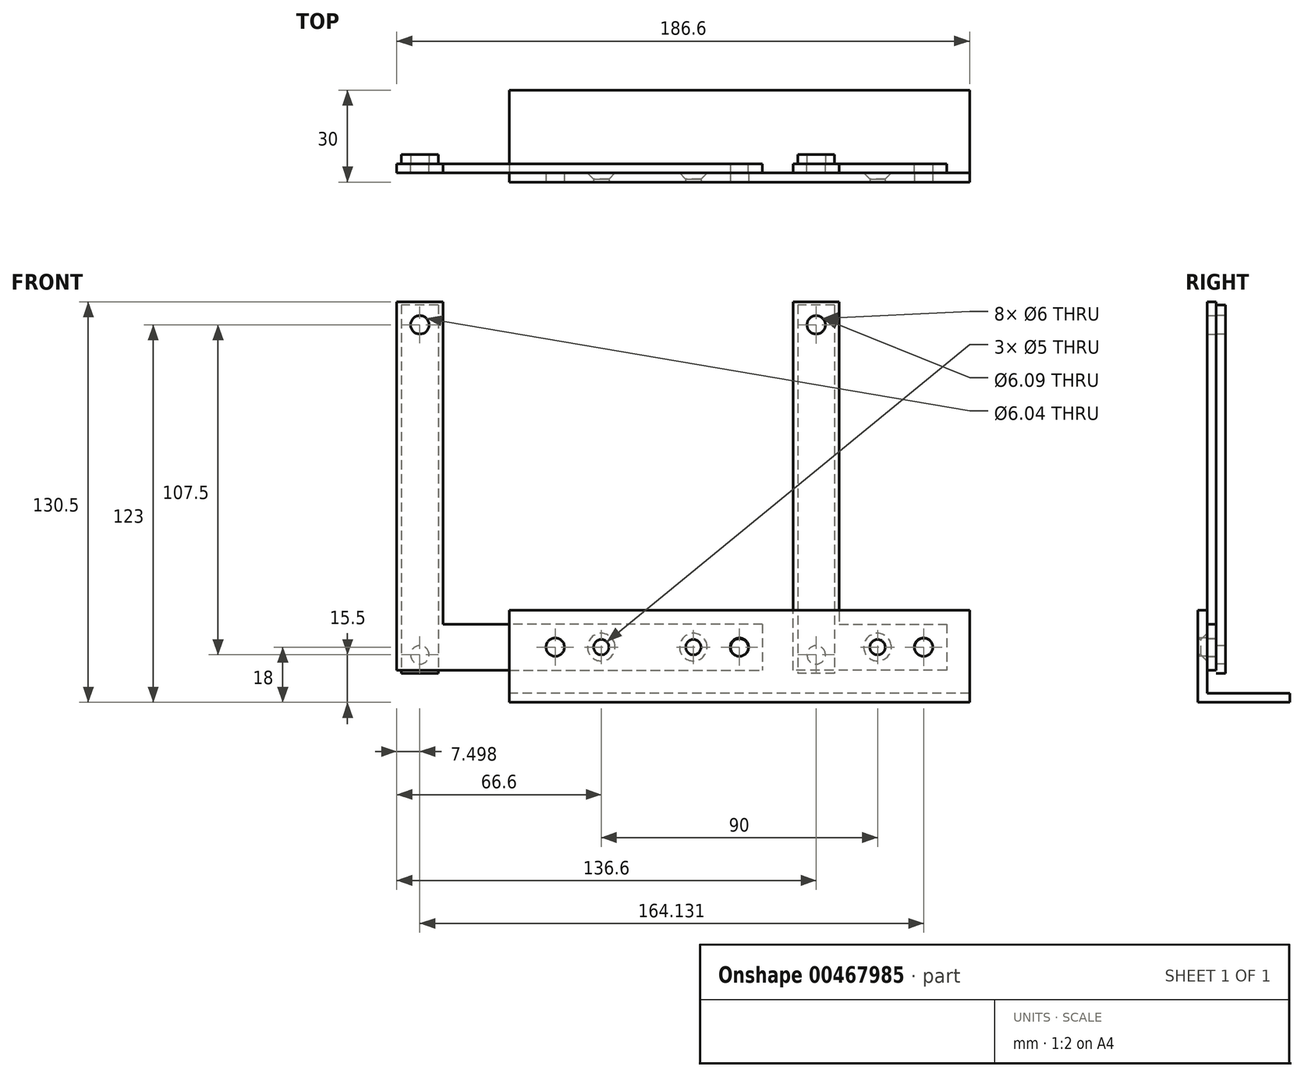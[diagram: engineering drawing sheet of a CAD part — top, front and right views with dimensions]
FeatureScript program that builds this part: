
annotation { "Feature Type Name" : "Feature", "Feature Type Description" : "" }
export const myFeature = defineFeature(function(context is Context, id is Id, definition is map)
    precondition{}
    {
        {
            var Q0;
            Q0=qCreatedBy(makeId("Right.planeOp"),FACE);
            var sketch = newSketch(context, id + "F0", { "sketchPlane" : qUnion([Q0])});
            skLineSegment(sketch, "E0", {"start": v(-6, 30) * mm, "end": v(-6, 0) * mm});
            skLineSegment(sketch, "E1", {"start": v(-6, 0) * mm, "end": v(24, 0) * mm});
            skLineSegment(sketch, "E2", {"start": v(24, 0) * mm, "end": v(24, 3) * mm});
            skLineSegment(sketch, "E3", {"start": v(24, 3) * mm, "end": v(-3, 3) * mm});
            skLineSegment(sketch, "E4", {"start": v(-3, 3) * mm, "end": v(-3, 30) * mm});
            skLineSegment(sketch, "E5", {"start": v(-3, 30) * mm, "end": v(-6, 30) * mm});
            skSolve(sketch);
        }
        {
            var Q0;
            Q0 = qSketchRegion(id + "F0", true);
            extrude(context, id + "F1", {"entities" : qUnion([Q0]), "depth" : 150 * mm});
        }
        {
            var Q0;
            Q0=qCreatedBy(makeId("Front.planeOp"),FACE);
            var sketch = newSketch(context, id + "F2", { "sketchPlane" : qUnion([Q0])});
            skCircle(sketch, "E6", {"center": v(135, 18) * mm, "radius": 3 * mm});
            skCircle(sketch, "E7", {"center": v(75, 18) * mm, "radius": 3 * mm});
            skCircle(sketch, "E8", {"center": v(15, 18) * mm, "radius": 3 * mm});
            skCircle(sketch, "E9", {"center": v(120, 18) * mm, "radius": 2.5 * mm});
            skCircle(sketch, "E10", {"center": v(30, 18) * mm, "radius": 2.5 * mm});
            skCircle(sketch, "E11", {"center": v(60, 18) * mm, "radius": 2.5 * mm});
            skSolve(sketch);
        }
        {
            var Q0;
            Q0 = qSketchRegion(id + "F2", true);
            extrude(context, id + "F3", {"entities" : qUnion([Q0]), "operationType" : NewBodyOperationType.REMOVE, "endBound" : BoundingType.SYMMETRIC, "oppositeDirection" : true, "depth" : 25 * mm});
        }
        {
            var Q0;
            Q0=makeQuery(id+"F3.boolean.opBoolean","INTERSECT",EDGE,{"derivedFrom":[makeQuery(id+"F1.opExtrude","SWEPT_FACE",FACE,{"disambiguationData":[OSD([sQuery(id+"F0.wireOp",EDGE,"E4")])]}),makeQuery(id+"F3.opExtrude","SWEPT_FACE",FACE,{"disambiguationData":[OSD([sQuery(id+"F2.wireOp",EDGE,"E11")])]})]});
            var Q1;
            Q1=makeQuery(id+"F3.boolean.opBoolean","INTERSECT",EDGE,{"derivedFrom":[makeQuery(id+"F1.opExtrude","SWEPT_FACE",FACE,{"disambiguationData":[OSD([sQuery(id+"F0.wireOp",EDGE,"E4")])]}),makeQuery(id+"F3.opExtrude","SWEPT_FACE",FACE,{"disambiguationData":[OSD([sQuery(id+"F2.wireOp",EDGE,"E10")])]})]});
            var Q2;
            Q2=makeQuery(id+"F3.boolean.opBoolean","INTERSECT",EDGE,{"derivedFrom":[makeQuery(id+"F1.opExtrude","SWEPT_FACE",FACE,{"disambiguationData":[OSD([sQuery(id+"F0.wireOp",EDGE,"E4")])]}),makeQuery(id+"F3.opExtrude","SWEPT_FACE",FACE,{"disambiguationData":[OSD([sQuery(id+"F2.wireOp",EDGE,"E9")])]})]});
            chamfer(context, id + "F4", {"entities" : qUnion([Q0, Q1, Q2]), "width" : 2 * mm, "tangentPropagation" : true});
        }
        {
            var Q0;
            Q0=qCreatedBy(makeId("Front.planeOp"),FACE);
            var sketch = newSketch(context, id + "F5", { "sketchPlane" : qUnion([Q0])});
            skLineSegment(sketch, "E12", {"start": v(142.5, 25.5) * mm, "end": v(142.5, 10.5) * mm});
            skLineSegment(sketch, "E13", {"start": v(142.5, 10.5) * mm, "end": v(92.5, 10.5) * mm});
            skLineSegment(sketch, "E14", {"start": v(92.5, 10.5) * mm, "end": v(92.5, 130.5) * mm});
            skLineSegment(sketch, "E15", {"start": v(92.5, 130.5) * mm, "end": v(107.5, 130.5) * mm});
            skLineSegment(sketch, "E16", {"start": v(107.5, 130.5) * mm, "end": v(107.5, 25.5) * mm});
            skLineSegment(sketch, "E17", {"start": v(107.5, 25.5) * mm, "end": v(142.5, 25.5) * mm});
            skCircle(sketch, "E18", {"center": v(135.03, 17.92) * mm, "radius": 3 * mm});
            skLineSegment(sketch, "E19", {"start": v(82.5, 25.5) * mm, "end": v(82.5, 10.5) * mm});
            skLineSegment(sketch, "E20", {"start": v(82.5, 25.5) * mm, "end": v(-21.6, 25.5) * mm});
            skLineSegment(sketch, "E21", {"start": v(-21.6, 25.5) * mm, "end": v(-21.6, 130.5) * mm});
            skLineSegment(sketch, "E22", {"start": v(-36.6, 130.5) * mm, "end": v(-36.6, 10.5) * mm});
            skLineSegment(sketch, "E23", {"start": v(-36.6, 10.5) * mm, "end": v(82.5, 10.5) * mm});
            skLineSegment(sketch, "E24", {"start": v(-21.6, 130.5) * mm, "end": v(-36.6, 130.5) * mm});
            skCircle(sketch, "E25", {"center": v(100, 123) * mm, "radius": 3 * mm});
            skCircle(sketch, "E26", {"center": v(-29.1, 123) * mm, "radius": 3 * mm});
            skCircle(sketch, "E27", {"center": v(75.01, 17.87) * mm, "radius": 2.9 * mm});
            skSolve(sketch);
        }
        {
            var Q0;
            Q0 = qSketchRegion(id + "F5", true);
            extrude(context, id + "F6", {"entities" : qUnion([Q0]), "depth" : 3 * mm});
        }
        {
            var Q0;
            Q0=qCreatedBy(makeId("Front.planeOp"),FACE);
            var sketch = newSketch(context, id + "F7", { "sketchPlane" : qUnion([Q0])});
            skLineSegment(sketch, "E28.bottom", {"start": v(106, 129.5) * mm, "end": v(94, 129.5) * mm});
            skLineSegment(sketch, "E28.top", {"start": v(106, 9.5) * mm, "end": v(94, 9.5) * mm});
            skLineSegment(sketch, "E28.left", {"start": v(106, 129.5) * mm, "end": v(106, 9.5) * mm});
            skLineSegment(sketch, "E28.right", {"start": v(94, 129.5) * mm, "end": v(94, 9.5) * mm});
            skLineSegment(sketch, "E29.bottom", {"start": v(-23.1, 129.5) * mm, "end": v(-35.1, 129.5) * mm});
            skLineSegment(sketch, "E29.top", {"start": v(-23.1, 9.5) * mm, "end": v(-35.1, 9.5) * mm});
            skLineSegment(sketch, "E29.left", {"start": v(-23.1, 129.5) * mm, "end": v(-23.1, 9.5) * mm});
            skLineSegment(sketch, "E29.right", {"start": v(-35.1, 129.5) * mm, "end": v(-35.1, 9.5) * mm});
            skCircle(sketch, "E30", {"center": v(100, 123) * mm, "radius": 3.05 * mm});
            skCircle(sketch, "E31", {"center": v(-29.1, 123) * mm, "radius": 3.02 * mm});
            skCircle(sketch, "E32", {"center": v(100, 15.5) * mm, "radius": 3 * mm});
            skCircle(sketch, "E33", {"center": v(-29.1, 15.5) * mm, "radius": 3 * mm});
            skSolve(sketch);
        }
        {
            var Q0;
            Q0 = qSketchRegion(id + "F7", true);
            extrude(context, id + "F8", {"entities" : qUnion([Q0]), "oppositeDirection" : true, "depth" : 3 * mm});
        }
    });
